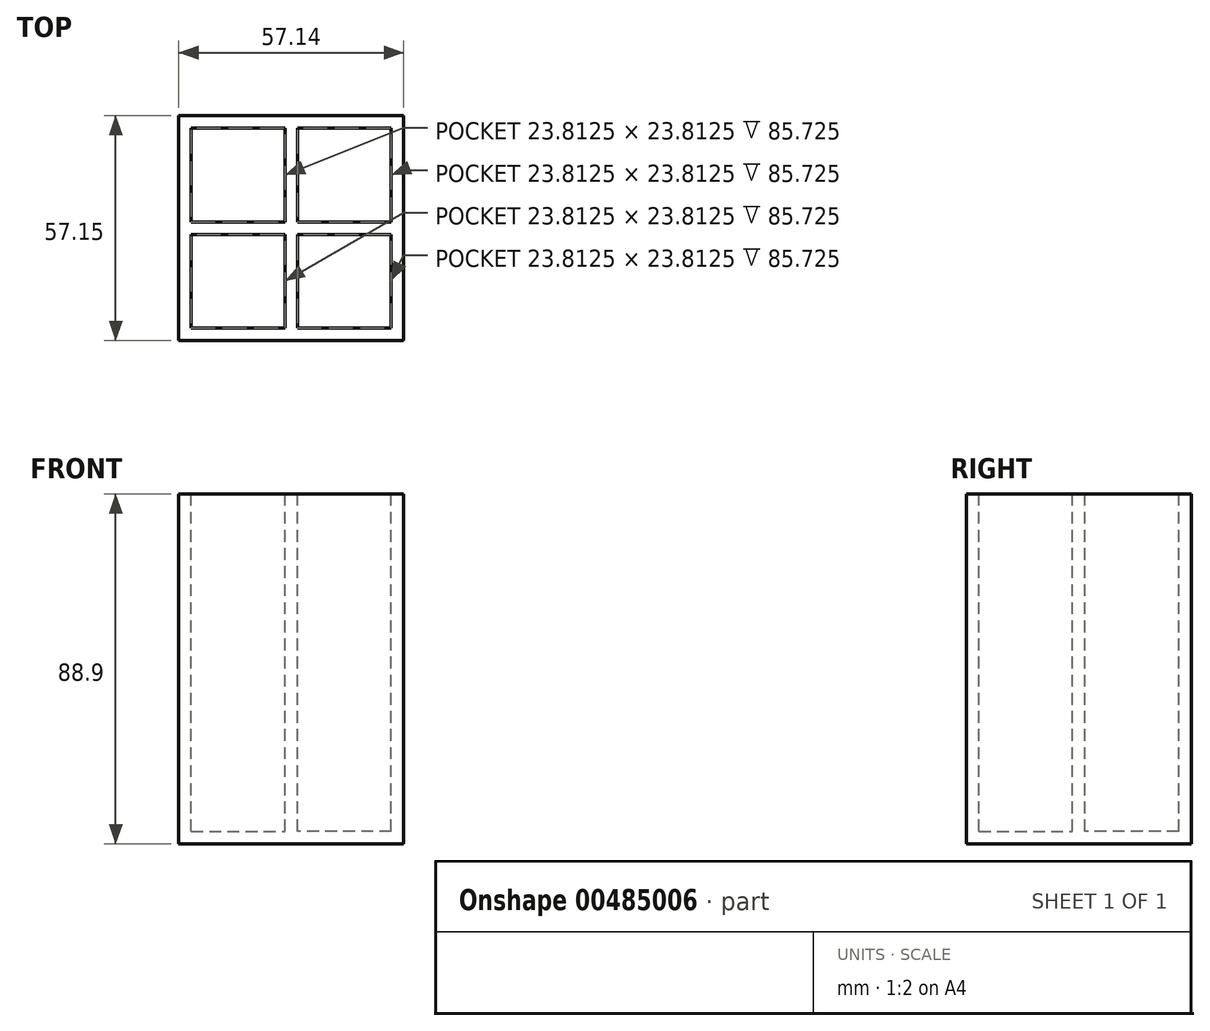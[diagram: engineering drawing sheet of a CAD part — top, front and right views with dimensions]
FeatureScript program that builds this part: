
annotation { "Feature Type Name" : "Feature", "Feature Type Description" : "" }
export const myFeature = defineFeature(function(context is Context, id is Id, definition is map)
    precondition{}
    {
        {
            var Q0;
            Q0=qCreatedBy(makeId("Front.planeOp"),FACE);
            var sketch = newSketch(context, id + "F0", { "sketchPlane" : qUnion([Q0])});
            skLineSegment(sketch, "E0.bottom", {"start": v(28.57, 44.45) * mm, "end": v(-28.58, 44.45) * mm});
            skLineSegment(sketch, "E0.top", {"start": v(28.58, -44.45) * mm, "end": v(-28.57, -44.45) * mm});
            skLineSegment(sketch, "E0.left", {"start": v(28.57, 44.45) * mm, "end": v(28.58, -44.45) * mm});
            skLineSegment(sketch, "E0.right", {"start": v(-28.58, 44.45) * mm, "end": v(-28.57, -44.45) * mm});
            skPoint(sketch, "E0.middle", {"position": v(0, 0) * mm});
            skSolve(sketch);
        }
        {
            var Q0;
            Q0 = qSketchRegion(id + "F0", true);
            extrude(context, id + "F1", {"entities" : qUnion([Q0]), "depth" : 57.15 * mm});
        }
        {
            var Q0;
            Q0=makeQuery(id+"F1.opExtrude","SWEPT_FACE",FACE,{"disambiguationData":[OSD([sQuery(id+"F0.wireOp",EDGE,"E0.bottom")])]});
            var sketch = newSketch(context, id + "F2", { "sketchPlane" : qUnion([Q0])});
            skLineSegment(sketch, "E1.bottom", {"start": v(-25.4, -3.18) * mm, "end": v(-1.59, -3.17) * mm});
            skLineSegment(sketch, "E1.top", {"start": v(-25.4, -26.99) * mm, "end": v(-1.59, -26.99) * mm});
            skLineSegment(sketch, "E1.left", {"start": v(-25.4, -3.18) * mm, "end": v(-25.4, -26.99) * mm});
            skLineSegment(sketch, "E1.right", {"start": v(-1.59, -3.17) * mm, "end": v(-1.59, -26.99) * mm});
            skSolve(sketch);
        }
        {
            var Q0;
            Q0=makeQuery(id+"F2.imprint","IMPRINT",FACE,{"disambiguationData":[TD([[makeQuery(id+"F2.imprint","IMPRINT",EDGE,{"derivedFrom":sQuery(id+"F2.wireOp",EDGE,"E1.bottom")}),1.0]])]});
            var sketch = newSketch(context, id + "F3", { "sketchPlane" : qUnion([Q0])});
            skLineSegment(sketch, "E2.bottom", {"start": v(25.4, -3.17) * mm, "end": v(1.59, -3.18) * mm});
            skLineSegment(sketch, "E2.top", {"start": v(25.4, -26.99) * mm, "end": v(1.59, -26.99) * mm});
            skLineSegment(sketch, "E2.left", {"start": v(25.4, -3.17) * mm, "end": v(25.4, -26.99) * mm});
            skLineSegment(sketch, "E2.right", {"start": v(1.59, -3.18) * mm, "end": v(1.59, -26.99) * mm});
            skSolve(sketch);
        }
        {
            var Q0;
            Q0 = qSketchRegion(id + "F2", true);
            extrude(context, id + "F4", {"entities" : qUnion([Q0]), "operationType" : NewBodyOperationType.REMOVE, "oppositeDirection" : true, "depth" : 85.72 * mm});
        }
        {
            var Q0;
            Q0 = qSketchRegion(id + "F3", true);
            extrude(context, id + "F5", {"entities" : qUnion([Q0]), "operationType" : NewBodyOperationType.REMOVE, "oppositeDirection" : true, "depth" : 85.72 * mm});
        }
        {
            var Q0;
            Q0=makeQuery(id+"F1.opExtrude","SWEPT_FACE",FACE,{"disambiguationData":[OSD([sQuery(id+"F0.wireOp",EDGE,"E0.bottom")])]});
            var sketch = newSketch(context, id + "F6", { "sketchPlane" : qUnion([Q0])});
            skLineSegment(sketch, "E3.bottom", {"start": v(-25.4, -53.98) * mm, "end": v(-1.59, -53.98) * mm});
            skLineSegment(sketch, "E3.top", {"start": v(-25.4, -30.16) * mm, "end": v(-1.59, -30.16) * mm});
            skLineSegment(sketch, "E3.left", {"start": v(-25.4, -53.98) * mm, "end": v(-25.4, -30.16) * mm});
            skLineSegment(sketch, "E3.right", {"start": v(-1.59, -53.98) * mm, "end": v(-1.59, -30.16) * mm});
            skSolve(sketch);
        }
        {
            var Q0;
            Q0 = qSketchRegion(id + "F6", true);
            extrude(context, id + "F7", {"entities" : qUnion([Q0]), "operationType" : NewBodyOperationType.REMOVE, "oppositeDirection" : true, "depth" : 85.72 * mm});
        }
        {
            var Q0;
            Q0=makeQuery(id+"F1.opExtrude","SWEPT_FACE",FACE,{"disambiguationData":[OSD([sQuery(id+"F0.wireOp",EDGE,"E0.bottom")])]});
            var sketch = newSketch(context, id + "F8", { "sketchPlane" : qUnion([Q0])});
            skLineSegment(sketch, "E4.bottom", {"start": v(25.4, -30.16) * mm, "end": v(1.59, -30.16) * mm});
            skLineSegment(sketch, "E4.top", {"start": v(25.4, -53.98) * mm, "end": v(1.59, -53.98) * mm});
            skLineSegment(sketch, "E4.left", {"start": v(25.4, -30.16) * mm, "end": v(25.4, -53.98) * mm});
            skLineSegment(sketch, "E4.right", {"start": v(1.59, -30.16) * mm, "end": v(1.59, -53.98) * mm});
            skSolve(sketch);
        }
        {
            var Q0;
            Q0 = qSketchRegion(id + "F8", true);
            extrude(context, id + "F9", {"entities" : qUnion([Q0]), "operationType" : NewBodyOperationType.REMOVE, "oppositeDirection" : true, "depth" : 85.72 * mm});
        }
    });
